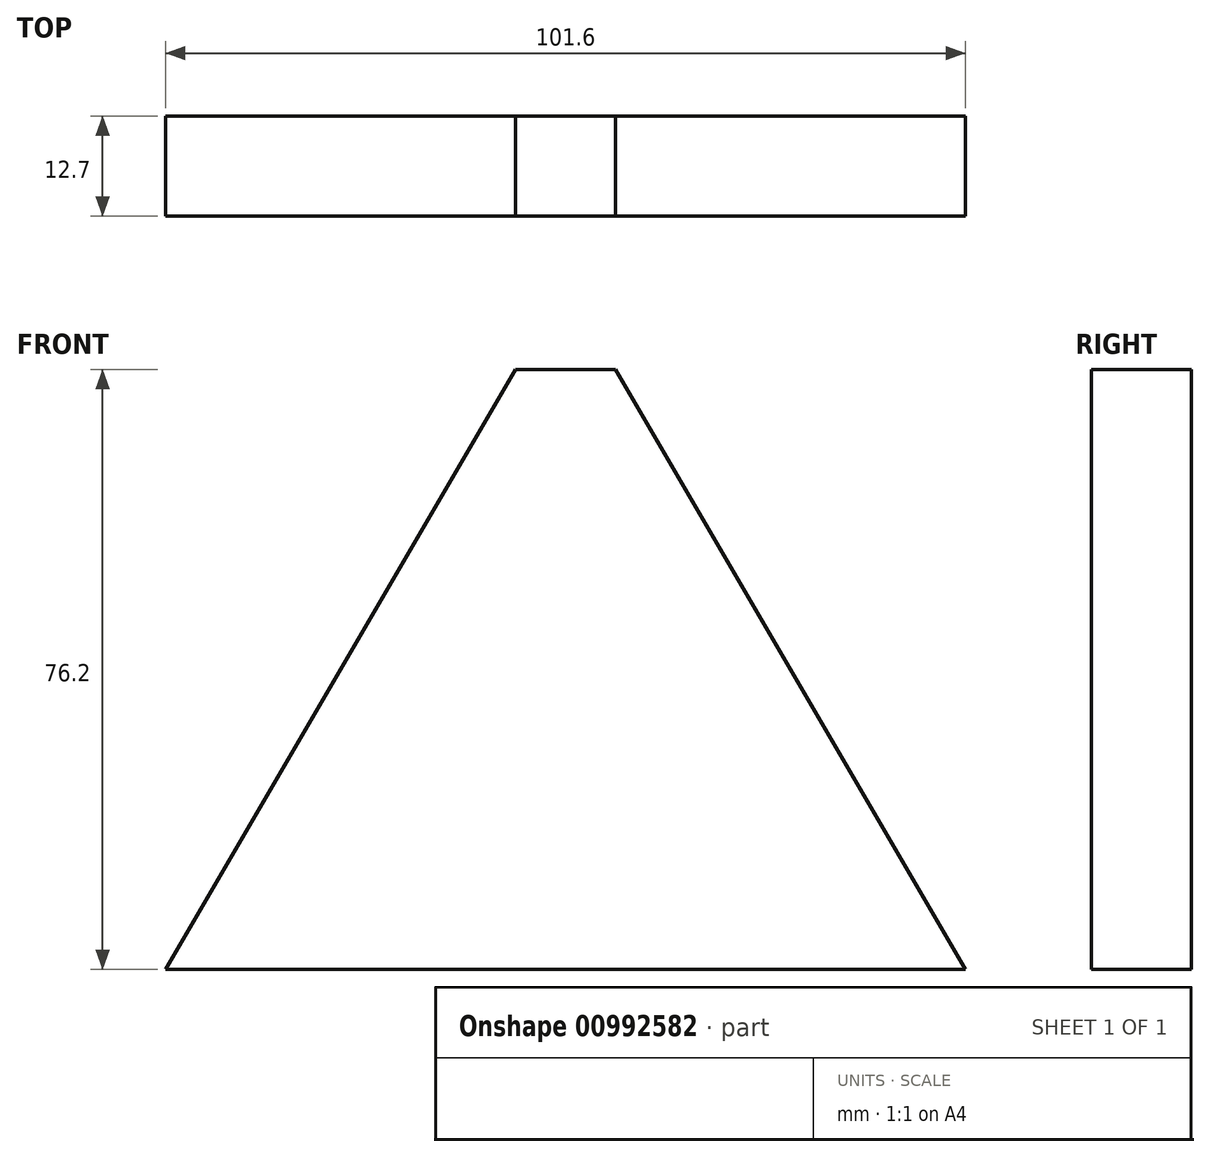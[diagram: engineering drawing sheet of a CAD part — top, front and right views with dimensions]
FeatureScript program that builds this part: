
annotation { "Feature Type Name" : "Feature", "Feature Type Description" : "" }
export const myFeature = defineFeature(function(context is Context, id is Id, definition is map)
    precondition{}
    {
        {
            var Q0;
            Q0=qCreatedBy(makeId("Front.planeOp"),FACE);
            var sketch = newSketch(context, id + "F0", { "sketchPlane" : qUnion([Q0])});
            skLineSegment(sketch, "E0", {"start": v(0, 0) * mm, "end": v(-6.35, 0) * mm});
            skLineSegment(sketch, "E1", {"start": v(-6.35, 0) * mm, "end": v(-50.8, -76.2) * mm});
            skLineSegment(sketch, "E2", {"start": v(-50.8, -76.2) * mm, "end": v(0, -76.2) * mm});
            skLineSegment(sketch, "E3.MirrorCS", {"start": v(0, 0) * mm, "end": v(6.35, 0) * mm});
            skLineSegment(sketch, "E4.MirrorCS", {"start": v(6.35, 0) * mm, "end": v(50.8, -76.2) * mm});
            skLineSegment(sketch, "E5.MirrorCS", {"start": v(50.8, -76.2) * mm, "end": v(0, -76.2) * mm});
            skSolve(sketch);
        }
        {
            var Q0;
            Q0=makeQuery(id+"F0.imprint","IMPRINT",FACE,{"disambiguationData":[TD([[makeQuery(id+"F0.imprint","IMPRINT",EDGE,{"derivedFrom":sQuery(id+"F0.wireOp",EDGE,"E0")}),1.0]])]});
            extrude(context, id + "F1", {"entities" : qUnion([Q0]), "depth" : 12.7 * mm, "offsetDistance" : 25.4 * mm});
        }
    });
